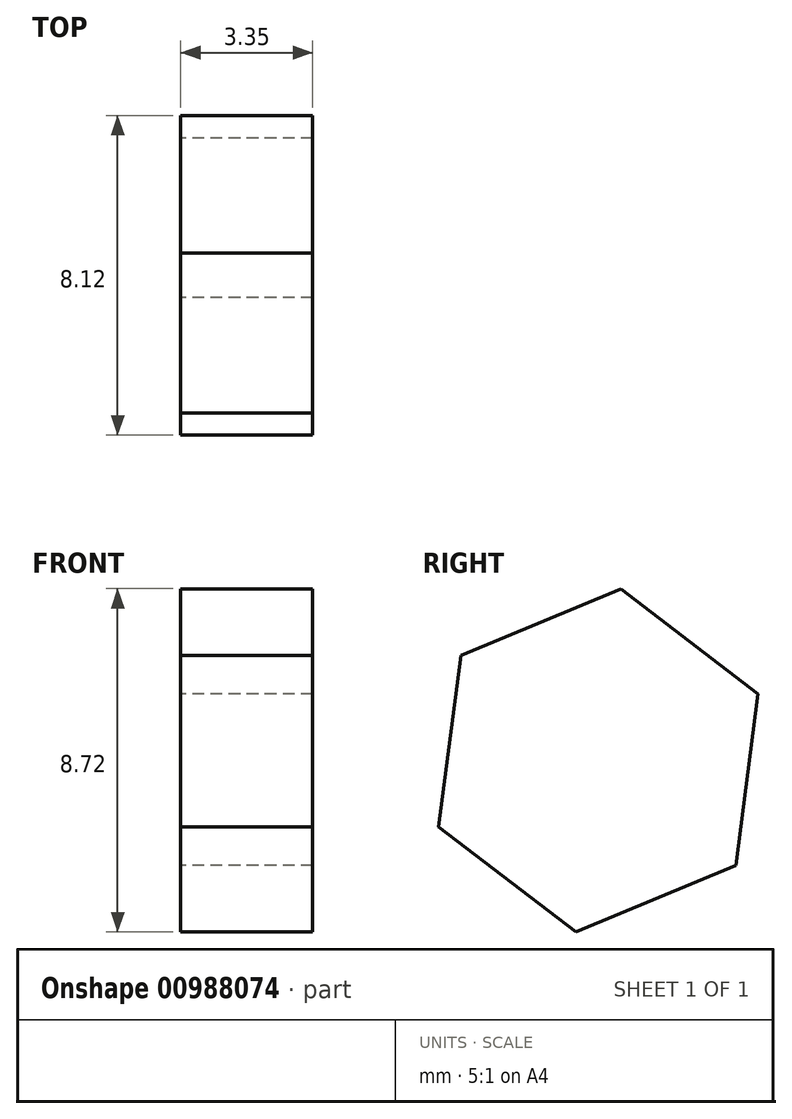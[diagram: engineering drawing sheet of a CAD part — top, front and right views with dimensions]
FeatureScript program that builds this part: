
annotation { "Feature Type Name" : "Feature", "Feature Type Description" : "" }
export const myFeature = defineFeature(function(context is Context, id is Id, definition is map)
    precondition{}
    {
        {
            var Q0;
            Q0=qCreatedBy(makeId("Right.planeOp"),FACE);
            var sketch = newSketch(context, id + "F0", { "sketchPlane" : qUnion([Q0])});
            skCircle(sketch, "E0.cCircle", {"center": v(0, 0) * mm, "radius": 4.4 * mm, "construction": true});
            skLineSegment(sketch, "E0.0", {"start": v(3.5, -2.67) * mm, "end": v(-0.57, -4.36) * mm});
            skLineSegment(sketch, "E0.1", {"start": v(-0.57, -4.36) * mm, "end": v(-4.06, -1.69) * mm});
            skLineSegment(sketch, "E0.2", {"start": v(-4.06, -1.69) * mm, "end": v(-3.5, 2.67) * mm});
            skLineSegment(sketch, "E0.3", {"start": v(-3.5, 2.67) * mm, "end": v(0.57, 4.36) * mm});
            skLineSegment(sketch, "E0.4", {"start": v(0.57, 4.36) * mm, "end": v(4.06, 1.69) * mm});
            skLineSegment(sketch, "E0.5", {"start": v(4.06, 1.69) * mm, "end": v(3.5, -2.67) * mm});
            skSolve(sketch);
        }
        {
            var Q0;
            Q0 = qSketchRegion(id + "F0", true);
            extrude(context, id + "F1", {"entities" : qUnion([Q0]), "depth" : 3.35 * mm, "offsetDistance" : 25.4 * mm});
        }
    });
